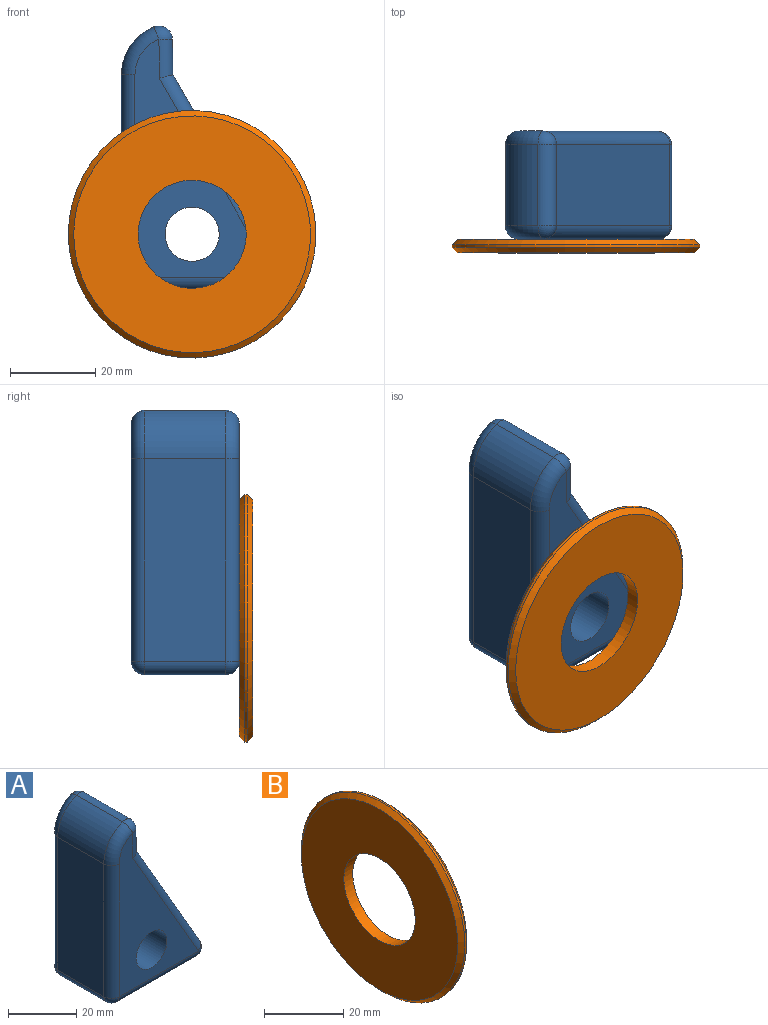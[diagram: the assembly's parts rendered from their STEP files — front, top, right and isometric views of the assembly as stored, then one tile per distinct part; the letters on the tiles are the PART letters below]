
ASSEMBLY  parts=2 mates=2
PART A: 27 faces, bbox 40.1x25.4x63 mm
  f0: plane 47.63x19.05mm, normal (-1,0,0), area 907.3mm2, adj f4,f11,f20,f25
  f1: plane 32.72x19.05mm, normal (0,0,-1), area 623.3mm2, adj f12,f13,f20,f21
  f2: plane 46.04x26.58mm, normal (0.87,0,0.5), area 1012.7mm2, adj f3,f7,f13,f14
  f3: plane 19.05x8.3mm, normal (1,0,0.01), area 158.2mm2, adj f2,f9,f18,f19
  f4: cylinder r=12.06mm len=19.05mm, axis (0,1,0), area 274.9mm2, adj f0,f10,f19,f24
  f5: plane 55.9x32.72mm, normal (0,-1,0), area 811.2mm2, adj f7,f9,f10,f11,f12,f26
  f6: plane 55.9x32.72mm, normal (0,1,0), area 811.2mm2, adj f14,f18,f21,f24,f25,f26
  f7: cylinder r=3.17mm len=48.35mm, axis (0.5,0,-0.87), area 266.6mm2, adj f2,f5,f8,f9
  f8: sphere r=3.17mm, area 21.1mm2, adj f7,f12,f13
  f9: cylinder r=3.17mm len=9.17mm, axis (0.01,0,-1), area 42.9mm2, adj f3,f5,f7,f15
  f10: torus R=8.89mm, axis (0,-1,0), area 65.1mm2, adj f4,f5,f11,f15
  f11: cylinder r=3.17mm len=47.63mm, axis (0,0,1), area 237.5mm2, adj f0,f5,f10,f16
  f12: cylinder r=3.17mm len=32.72mm, axis (-1,0,0), area 163.2mm2, adj f1,f5,f8,f16
  f13: cylinder r=3.17mm len=19.05mm, axis (0,1,0), area 126.7mm2, adj f1,f2,f8,f17
  f14: cylinder r=3.17mm len=48.35mm, axis (-0.5,0,0.87), area 266.6mm2, adj f2,f6,f17,f18
  f15: sphere r=3.17mm, area 19.5mm2, adj f9,f10,f19
  f16: sphere r=3.17mm, area 15.8mm2, adj f11,f12,f20
  f17: sphere r=3.17mm, area 21.1mm2, adj f13,f14,f21
  f18: cylinder r=3.17mm len=9.17mm, axis (-0.01,0,1), area 42.9mm2, adj f3,f6,f14,f22
  f19: cylinder r=3.17mm len=19.05mm, axis (0,1,0), area 117.1mm2, adj f3,f4,f15,f22
  f20: cylinder r=3.17mm len=19.05mm, axis (0,-1,0), area 95mm2, adj f0,f1,f16,f23
  f21: cylinder r=3.17mm len=32.72mm, axis (1,0,0), area 163.2mm2, adj f1,f6,f17,f23
  f22: sphere r=3.17mm, area 19.5mm2, adj f18,f19,f24
  f23: sphere r=3.17mm, area 15.8mm2, adj f20,f21,f25
  f24: torus R=8.89mm, axis (0,-1,0), area 65.1mm2, adj f4,f6,f22,f25
  f25: cylinder r=3.17mm len=47.63mm, axis (0,0,-1), area 237.5mm2, adj f0,f6,f23,f24
  f26: cylinder r=6.35mm len=25.4mm, axis (0,-1,0), area 1013.4mm2, adj f5,f6
PART B: 6 faces, bbox 3.2x58.2x58.2 mm
  f0: cylinder r=12.7mm len=25.4mm, axis (-1,0,0), area 253.4mm2, adj f2,f3
  f1: cylinder r=29.1mm len=58.2mm, axis (-1,0,0), area 116.1mm2, adj f4,f5
  f2: plane 55.66x55.66mm, normal (1,0,0), area 1926mm2, adj f0,f5
  f3: plane 55.66x55.66mm, normal (-1,0,0), area 1926mm2, adj f0,f4
  f4: cone r=29.1mm half-angle=45deg, axis (1,0,0), area 321.2mm2, adj f1,f3
  f5: cone r=27.83mm half-angle=45deg, axis (-1,0,0), area 321.2mm2, adj f1,f2
PLACE A t=(-27.14,-13.23,6.54)mm
PLACE B rot(axis=(-0.58,0.58,-0.58),120deg) t=(-10.53,-38.63,19.83)mm
MATE planar A.f5 <-> B.f1  axis (0,-1,0) through (-13.51,-38.63,30.41)mm
MATE cylindrical B.f0 <-> A.f26  axis (0,-1,0) through (-10.53,-41.81,19.83)mm
